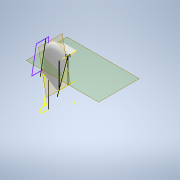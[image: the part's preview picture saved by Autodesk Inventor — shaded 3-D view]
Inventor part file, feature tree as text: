
AUTODESK INVENTOR PART (.ipt)
format: ipt  version: 2022 (Build 260153000, 153)  size: 1,577,984 bytes
history: native  units: mm
features: sketch x18, reference x18, other x13, extrude x12, fillet x12, projected_geometry x9, chamfer x3, loft x1, revolve x1
ambient origin geometry x8: Origin, YZ Plane, XZ Plane, XY Plane, X Axis, Y Axis, Z Axis, Center Point
bodies: Body1 (feature_tree)
feature tree (87):
  other  "Твердое тело1"
  other  "РабТочка1"
  extrude  "Выдавливание1"  Depth=30.0mm TaperAngle=0.0deg
  extrude  "Выдавливание2"  Depth=60.0mm TaperAngle=0.0deg
  sketch  "Эскиз4"
  sketch  "Эскиз5"
  sketch  "Эскиз6"
  extrude  "Выдавливание4"  Depth=0.25mm
  sketch  "Эскиз8"
  other  "РабПлоскость1"
  loft  "Лофт8"
  fillet  "Сопряжение5"  Radius=0.2mm
  extrude  "Выдавливание5"  Depth=0.5mm
  revolve  "Вращение1"
  fillet  "Сопряжение6"  Radius=2.0mm
  fillet  "Сопряжение7"  Radius=8.0mm
  other  "РабПлоскость2"
  sketch  "Эскиз13"
  extrude  "Выдавливание6"  Depth=2.0mm
  extrude  "Выдавливание7"  Depth=4.0mm
  fillet  "Сопряжение8"  Radius=4.0mm
  extrude  "Выдавливание8"  Depth=15.0mm TaperAngle=0.0deg
  fillet  "Сопряжение9"  [1 undecoded]
  extrude  "Выдавливание9"  Depth=4.0mm
  fillet  "Сопряжение10"  Radius=6.0mm
  fillet  "Сопряжение11"  Radius=0.3mm
  extrude  "Выдавливание10"  Depth=10.0mm TaperAngle=0.0deg
  extrude  "Выдавливание11"  Depth=3.0mm TaperAngle=0.0deg
  chamfer  "Фаска1"  Distance=2.0mm
  chamfer  "Фаска2"  Distance=5.0mm
  fillet  "Сопряжение12"  Radius=9.0mm
  fillet  "Сопряжение13"  Radius=11.0mm
  fillet  "Сопряжение14"  Radius=1.5mm
  fillet  "Сопряжение15"  Radius=4.0mm
  sketch  "Эскиз19"
  other  "РабПлоскость3"
  extrude  "Выдавливание12"  Depth=0.75mm
  chamfer  "Фаска3"  Distance=0.8mm
  extrude  "Выдавливание13"  Depth=0.8mm
  fillet  "Сопряжение16"  Radius=1.5mm
  sketch  "Эскиз1"
  reference  "Ссылка1"
  reference  "Ссылка2"
  reference  "Ссылка3"
  reference  "Ссылка4"
  sketch  "Эскиз2"
  reference  "Ссылка5"
  projected_geometry  "Спроецированная петля1"
  reference  "Ссылка6"
  reference  "Ссылка11"
  reference  "Ссылка13"
  sketch  "Эскиз7"
  reference  "Ссылка15"
  reference  "Ссылка16"
  reference  "Ссылка17"
  reference  "Ссылка18"
  reference  "Ссылка19"
  projected_geometry  "Спроецированная петля13"
  reference  "Ссылка22"
  sketch  "Эскиз9"
  projected_geometry  "Спроецированная петля14"
  sketch  "Эскиз11"
  sketch  "Эскиз12"
  projected_geometry  "Спроецированная петля18"
  reference  "Ссылка23"
  sketch  "Эскиз14"
  sketch  "Эскиз15"
  reference  "Ссылка24"
  sketch  "Эскиз16"
  projected_geometry  "Спроецированная петля19"
  projected_geometry  "Спроецированная петля20"
  sketch  "Эскиз17"
  reference  "Ссылка25"
  projected_geometry  "Спроецированная петля21"
  sketch  "Эскиз18"
  projected_geometry  "Спроецированная петля22"
  reference  "Ссылка26"
  projected_geometry  "Спроецированная петля23"
  sketch  "Эскиз20"
  other  "<userpath>\Documents\Git\MZCAT_2024\MZCAT_4.iam"
  other  "MZCAT_4.iam"
  other  "back_diffuser:1"
  other  "CAT_protector:1"
  other  "magazine_fixator:1"
  other  "vydacha_slide:1"
  other  "back_led_board:1"
  other  "antenna:2"
note: 1 required parameter value undecoded (feature->parameter linkage not recoverable at this tier; creation-order binding heuristic only, values carry confidence <= 0.55)
